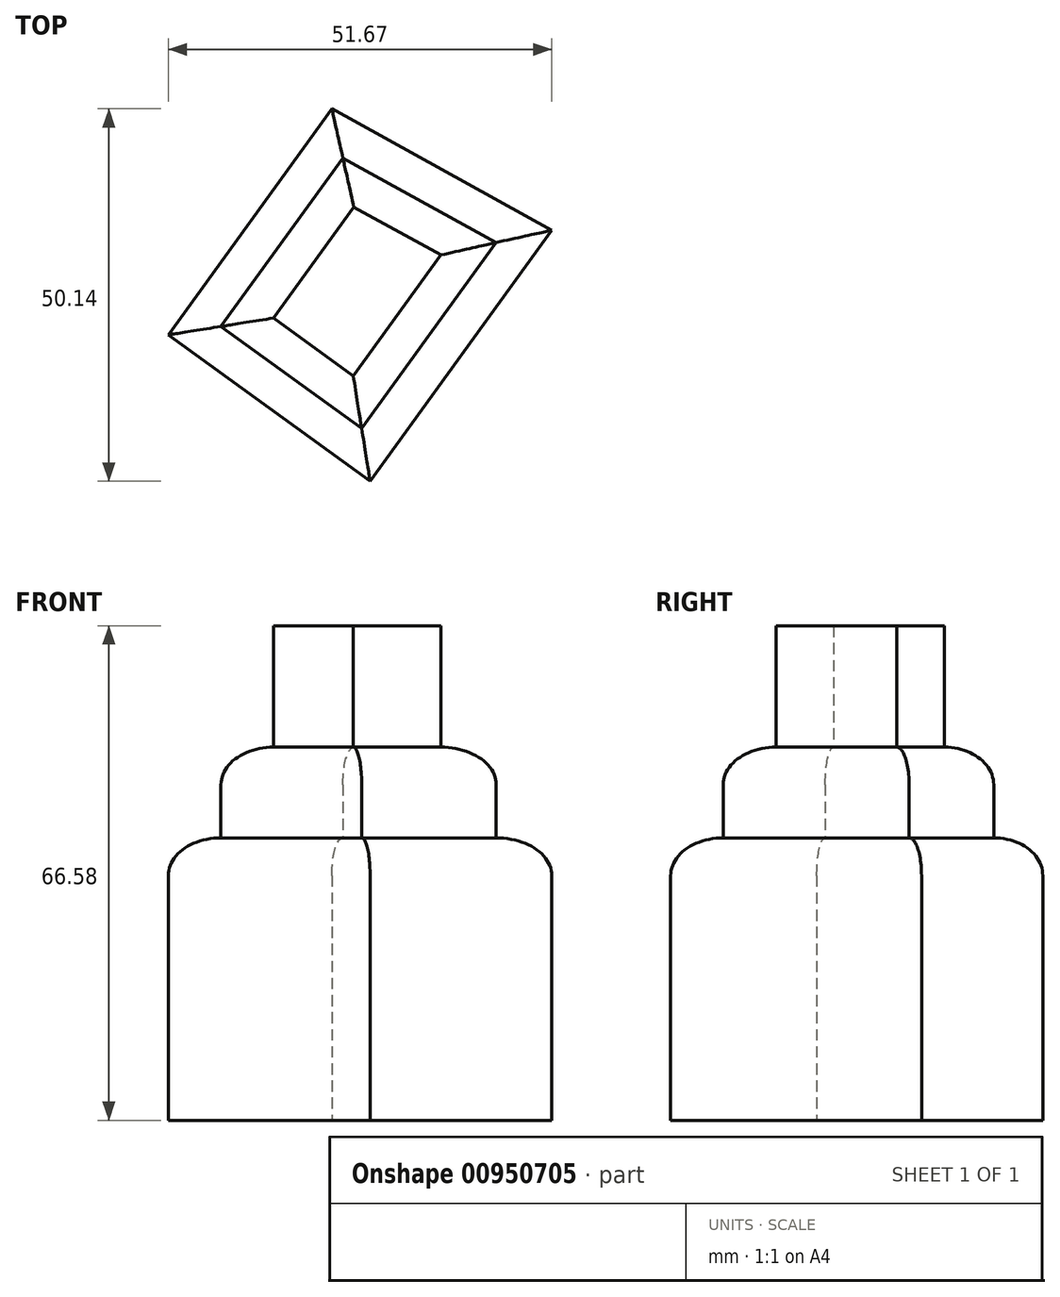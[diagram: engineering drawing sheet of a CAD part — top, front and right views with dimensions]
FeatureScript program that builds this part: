
annotation { "Feature Type Name" : "Feature", "Feature Type Description" : "" }
export const myFeature = defineFeature(function(context is Context, id is Id, definition is map)
    precondition{}
    {
        {
            var Q0;
            Q0=qCreatedBy(makeId("Top.planeOp"),FACE);
            var sketch = newSketch(context, id + "F0", { "sketchPlane" : qUnion([Q0])});
            skLineSegment(sketch, "E0", {"start": v(14.25, 14.4) * mm, "end": v(-7.8, -16.05) * mm});
            skLineSegment(sketch, "E1", {"start": v(-7.8, -16.05) * mm, "end": v(19.4, -35.74) * mm});
            skLineSegment(sketch, "E2", {"start": v(19.4, -35.74) * mm, "end": v(43.87, -1.94) * mm});
            skLineSegment(sketch, "E3", {"start": v(43.87, -1.94) * mm, "end": v(14.25, 14.4) * mm});
            skSolve(sketch);
        }
        {
            var Q0;
            Q0=makeQuery(id+"F0.imprint","IMPRINT",FACE,{"disambiguationData":[TD([[makeQuery(id+"F0.imprint","IMPRINT",EDGE,{"derivedFrom":sQuery(id+"F0.wireOp",EDGE,"E0")}),1.0]])]});
            extrude(context, id + "F1", {"entities" : qUnion([Q0]), "depth" : 38.04 * mm, "offsetDistance" : 25.4 * mm});
        }
        {
            var Q0;
            Q0=makeQuery(id+"F1.opExtrude","CAP_FACE",FACE,{"disambiguationData":[OSD([sQuery(id+"F0.wireOp",EDGE,"E0"),sQuery(id+"F0.wireOp",EDGE,"E1"),sQuery(id+"F0.wireOp",EDGE,"E2"),sQuery(id+"F0.wireOp",EDGE,"E3")])],"isStart":false});
            fillet(context, id + "F2", {"entities" : qUnion([Q0]), "radius" : 5.08 * mm, "tangentPropagation" : true, "allowEdgeOverflow" : false});
        }
        {
            var Q0;
            Q0=makeQuery(id+"F1.opExtrude","CAP_FACE",FACE,{"disambiguationData":[OSD([sQuery(id+"F0.wireOp",EDGE,"E0"),sQuery(id+"F0.wireOp",EDGE,"E1"),sQuery(id+"F0.wireOp",EDGE,"E2"),sQuery(id+"F0.wireOp",EDGE,"E3")])],"isStart":false});
            extrude(context, id + "F3", {"entities" : qUnion([Q0]), "operationType" : NewBodyOperationType.ADD, "depth" : 12.23 * mm, "offsetDistance" : 25.4 * mm});
        }
        {
            var Q0;
            {var subQ0=sQuery(id+"F0.wireOp",EDGE,"E3");var subQ1=sQuery(id+"F0.wireOp",EDGE,"E2");var subQ2=sQuery(id+"F0.wireOp",EDGE,"E1");var subQ3=sQuery(id+"F0.wireOp",EDGE,"E0");Q0=makeQuery(id+"F3.opExtrude","CAP_EDGE",EDGE,{"disambiguationData":[OSD([subQ3,subQ2,subQ1,subQ0]),TDD([makeQuery(id+"F2.opFillet","BLEND_EDGE",EDGE,{"blendedFrom":[makeQuery(id+"F1.opExtrude","CAP_EDGE",EDGE,{"disambiguationData":[OSD([subQ3])],"isStart":false}),makeQuery(id+"F1.opExtrude","CAP_FACE",FACE,{"disambiguationData":[OSD([subQ3,subQ2,subQ1,subQ0])],"isStart":false})],"blendedInto":[makeQuery(id+"F1.opExtrude","CAP_FACE",FACE,{"disambiguationData":[OSD([subQ3,subQ2,subQ1,subQ0])],"isStart":false})]})])],"isStart":false});}
            var Q1;
            {var subQ0=sQuery(id+"F0.wireOp",EDGE,"E3");var subQ1=sQuery(id+"F0.wireOp",EDGE,"E2");var subQ2=sQuery(id+"F0.wireOp",EDGE,"E1");var subQ3=sQuery(id+"F0.wireOp",EDGE,"E0");Q1=makeQuery(id+"F3.opExtrude","CAP_EDGE",EDGE,{"disambiguationData":[OSD([subQ3,subQ2,subQ1,subQ0]),TDD([makeQuery(id+"F2.opFillet","BLEND_EDGE",EDGE,{"blendedFrom":[makeQuery(id+"F1.opExtrude","CAP_EDGE",EDGE,{"disambiguationData":[OSD([subQ1])],"isStart":false}),makeQuery(id+"F1.opExtrude","CAP_FACE",FACE,{"disambiguationData":[OSD([subQ3,subQ2,subQ1,subQ0])],"isStart":false})],"blendedInto":[makeQuery(id+"F1.opExtrude","CAP_FACE",FACE,{"disambiguationData":[OSD([subQ3,subQ2,subQ1,subQ0])],"isStart":false})]})])],"isStart":false});}
            var Q2;
            {var subQ0=sQuery(id+"F0.wireOp",EDGE,"E3");var subQ1=sQuery(id+"F0.wireOp",EDGE,"E2");var subQ2=sQuery(id+"F0.wireOp",EDGE,"E1");var subQ3=sQuery(id+"F0.wireOp",EDGE,"E0");Q2=makeQuery(id+"F3.opExtrude","CAP_EDGE",EDGE,{"disambiguationData":[OSD([subQ3,subQ2,subQ1,subQ0]),TDD([makeQuery(id+"F2.opFillet","BLEND_EDGE",EDGE,{"blendedFrom":[makeQuery(id+"F1.opExtrude","CAP_EDGE",EDGE,{"disambiguationData":[OSD([subQ2])],"isStart":false}),makeQuery(id+"F1.opExtrude","CAP_FACE",FACE,{"disambiguationData":[OSD([subQ3,subQ2,subQ1,subQ0])],"isStart":false})],"blendedInto":[makeQuery(id+"F1.opExtrude","CAP_FACE",FACE,{"disambiguationData":[OSD([subQ3,subQ2,subQ1,subQ0])],"isStart":false})]})])],"isStart":false});}
            var Q3;
            {var subQ0=sQuery(id+"F0.wireOp",EDGE,"E3");var subQ1=sQuery(id+"F0.wireOp",EDGE,"E2");var subQ2=sQuery(id+"F0.wireOp",EDGE,"E1");var subQ3=sQuery(id+"F0.wireOp",EDGE,"E0");Q3=makeQuery(id+"F3.opExtrude","CAP_EDGE",EDGE,{"disambiguationData":[OSD([subQ3,subQ2,subQ1,subQ0]),TDD([makeQuery(id+"F2.opFillet","BLEND_EDGE",EDGE,{"blendedFrom":[makeQuery(id+"F1.opExtrude","CAP_EDGE",EDGE,{"disambiguationData":[OSD([subQ0])],"isStart":false}),makeQuery(id+"F1.opExtrude","CAP_FACE",FACE,{"disambiguationData":[OSD([subQ3,subQ2,subQ1,subQ0])],"isStart":false})],"blendedInto":[makeQuery(id+"F1.opExtrude","CAP_FACE",FACE,{"disambiguationData":[OSD([subQ3,subQ2,subQ1,subQ0])],"isStart":false})]})])],"isStart":false});}
            fillet(context, id + "F4", {"entities" : qUnion([Q0, Q1, Q2, Q3]), "radius" : 5.08 * mm, "tangentPropagation" : true, "allowEdgeOverflow" : false});
        }
        {
            var Q0;
            Q0=makeQuery(id+"F3.opExtrude","CAP_FACE",FACE,{"disambiguationData":[OSD([sQuery(id+"F0.wireOp",EDGE,"E0"),sQuery(id+"F0.wireOp",EDGE,"E1"),sQuery(id+"F0.wireOp",EDGE,"E2"),sQuery(id+"F0.wireOp",EDGE,"E3")])],"isStart":false});
            extrude(context, id + "F5", {"entities" : qUnion([Q0]), "operationType" : NewBodyOperationType.ADD, "depth" : 7.34 * mm, "offsetDistance" : 25.4 * mm});
        }
        {
            var Q0;
            Q0=makeQuery(id+"F5.opExtrude","CAP_FACE",FACE,{"disambiguationData":[OSD([sQuery(id+"F0.wireOp",EDGE,"E0"),sQuery(id+"F0.wireOp",EDGE,"E1"),sQuery(id+"F0.wireOp",EDGE,"E2"),sQuery(id+"F0.wireOp",EDGE,"E3")])],"isStart":false});
            extrude(context, id + "F6", {"entities" : qUnion([Q0]), "operationType" : NewBodyOperationType.ADD, "depth" : 8.97 * mm, "offsetDistance" : 25.4 * mm});
        }
    });
